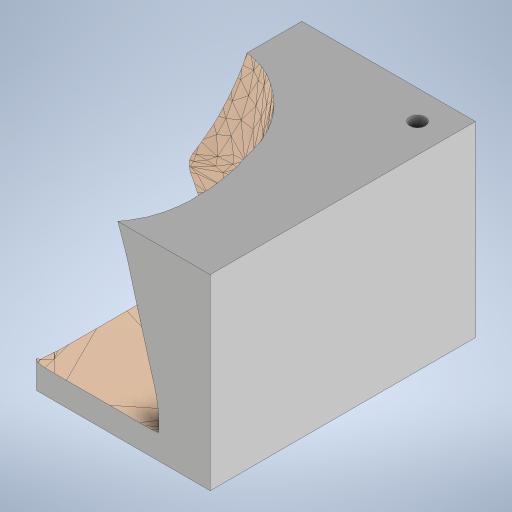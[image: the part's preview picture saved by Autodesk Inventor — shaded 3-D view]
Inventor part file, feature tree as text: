
AUTODESK INVENTOR PART (.ipt)
format: ipt  version: 2024 (Build 280153000, 153)  size: 10,769,408 bytes
history: native  units: mm
features: other x6, sketch x6, extrude x5, plane x2
ambient origin geometry x8: Origin, YZ Plane, XZ Plane, XY Plane, X Axis, Y Axis, Z Axis, Center Point
bodies: Body1 (feature_tree)
feature tree (19):
  other  "M.ipt"
  plane  "Plano de trabajo1"
  extrude  "Extrusión1"  [1 undecoded]
  other  "Combinar1"
  sketch  "Boceto3"  dims[d2=550.0mm d3=520.0mm]
  sketch  "Boceto4"  dims[d4=550.0mm d5=0.0mm d6=129.8482mm]
  plane  "Plano de trabajo2"
  sketch  "Boceto5"  dims[d17=180.0mm d18=180.0mm]
  extrude  "Extrusión2"  Depth=520.0mm
  extrude  "Extrusión3"  Depth=129.8482mm
  extrude  "Extrusión4"  Depth=180.0mm
  extrude  "Extrusión5"  Depth=180.0mm
  other  "Sólido1::M.ipt"
  other  "OperaciónIdentificador1"
  sketch  "Boceto1"  dims[d0=25.0mm d1=-365.0mm]
  other  "Sólido2"
  sketch  "Boceto6"  dims[d22=326.0mm d23=180.0mm]
  sketch  "Boceto7"  dims[d24=180.0mm d25=180.0mm d26=10.0mm d27=0.0mm d28=1000.0mm d29=0.0mm d30=30.0mm d31=30.0mm d32=16.0mm d33=16.0mm d34=0.0mm d35=30.0mm d36=30.0mm d37=16.0mm d38=16.0mm d39=0.0mm d14=0.5mm d15=0.872665mm d16=0.5mm d19=0.5mm d20=0.872665mm d21=0.5mm]
  other  "Sólido1"
note: 1 required parameter value undecoded (feature->parameter linkage not recoverable at this tier; creation-order binding heuristic only, values carry confidence <= 0.55)
